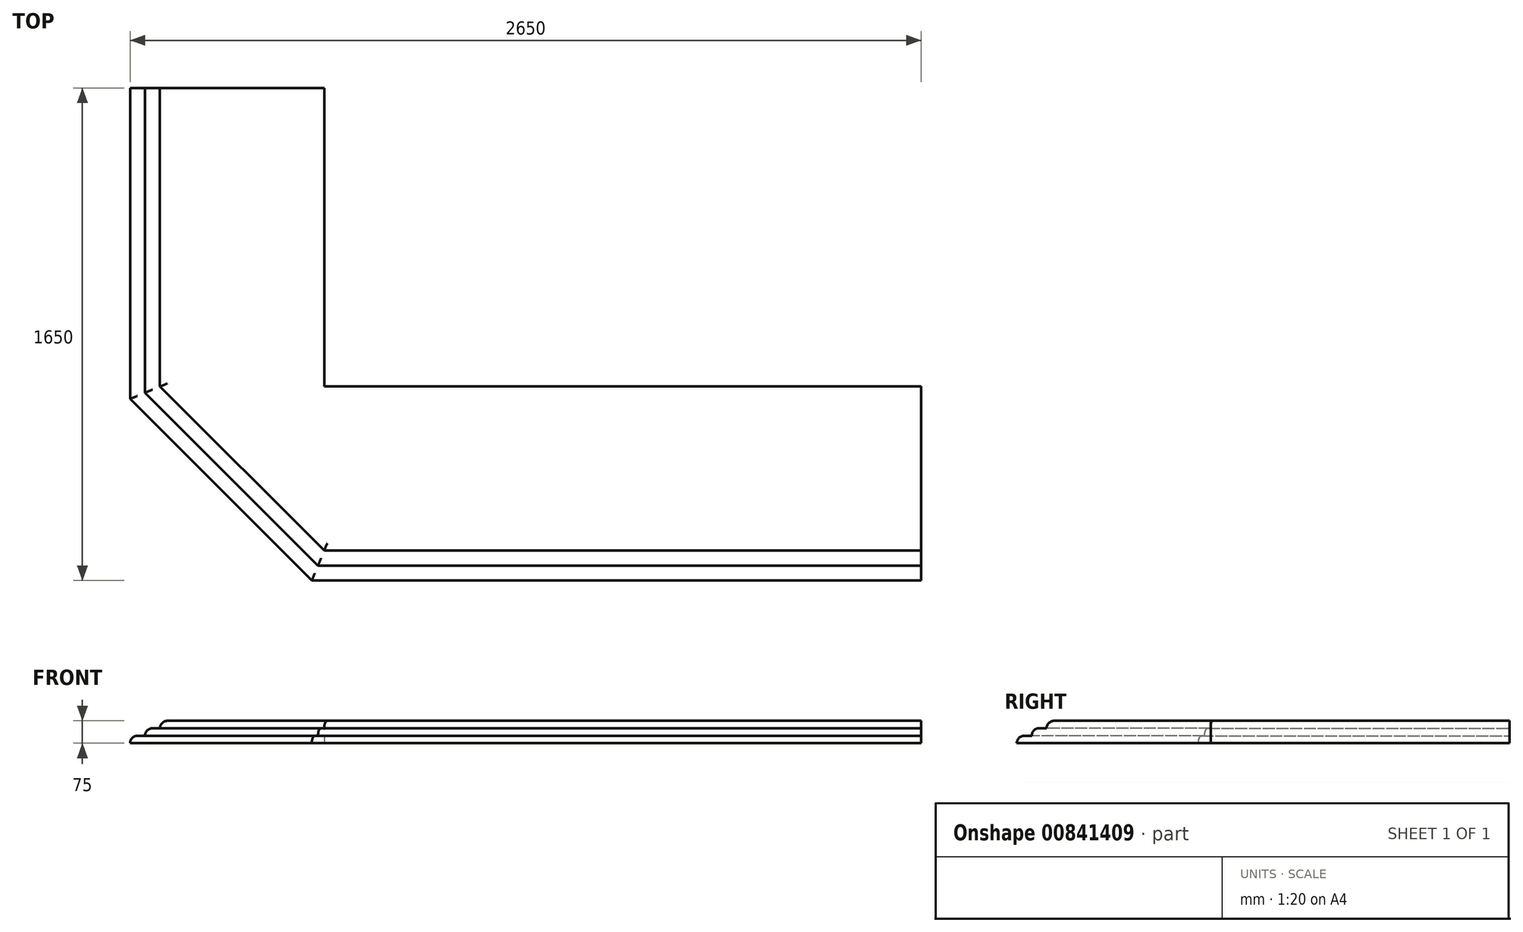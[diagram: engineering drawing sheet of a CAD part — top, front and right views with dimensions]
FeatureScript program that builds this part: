
annotation { "Feature Type Name" : "Feature", "Feature Type Description" : "" }
export const myFeature = defineFeature(function(context is Context, id is Id, definition is map)
    precondition{}
    {
        {
            var Q0;
            Q0=qCreatedBy(makeId("Top.planeOp"),FACE);
            var sketch = newSketch(context, id + "F0", { "sketchPlane" : qUnion([Q0])});
            skLineSegment(sketch, "E0.right", {"start": v(-1000, 500) * mm, "end": v(-1000, -500) * mm});
            skPoint(sketch, "E0.middle", {"position": v(0, 0) * mm});
            skLineSegment(sketch, "E1.bottom", {"start": v(-1000, -1050) * mm, "end": v(1000, -1050) * mm});
            skLineSegment(sketch, "E1.left", {"start": v(-1550, -500) * mm, "end": v(-1550, 500) * mm});
            skLineSegment(sketch, "E2", {"start": v(-1000, 500) * mm, "end": v(-1550, 500) * mm});
            skLineSegment(sketch, "E3", {"start": v(1000, -500) * mm, "end": v(1000, -1050) * mm});
            skLineSegment(sketch, "E4", {"start": v(1000, -500) * mm, "end": v(-1000, -500) * mm});
            skLineSegment(sketch, "E5", {"start": v(-1550, -500) * mm, "end": v(-1000, -1050) * mm});
            skPoint(sketch, "E6.orphan", {"position": v(-1550, 1050) * mm});
            skPoint(sketch, "E1.right.end.orphan", {"position": v(1550, 1050) * mm});
            skPoint(sketch, "E7.orphan", {"position": v(1550, -1050) * mm});
            skPoint(sketch, "E0.left.start.orphan", {"position": v(1000, 500) * mm});
            skPoint(sketch, "E8.orphan", {"position": v(-1550, -1050) * mm});
            skSolve(sketch);
        }
        {
            var Q0;
            Q0 = qSketchRegion(id + "F0", true);
            extrude(context, id + "F1", {"entities" : qUnion([Q0]), "depth" : 25 * mm, "offsetDistance" : 25 * mm});
        }
        {
            var Q0;
            Q0=makeQuery(id+"F1.opExtrude","CAP_FACE",FACE,{"disambiguationData":[OSD([sQuery(id+"F0.wireOp",EDGE,"E0.right"),sQuery(id+"F0.wireOp",EDGE,"E1.bottom"),sQuery(id+"F0.wireOp",EDGE,"E1.left"),sQuery(id+"F0.wireOp",EDGE,"E2"),sQuery(id+"F0.wireOp",EDGE,"E3"),sQuery(id+"F0.wireOp",EDGE,"E4"),sQuery(id+"F0.wireOp",EDGE,"E5")])],"isStart":true});
            var sketch = newSketch(context, id + "F2", { "sketchPlane" : qUnion([Q0])});
            skLineSegment(sketch, "E9.0", {"start": v(-1600, 520.71) * mm, "end": v(-1600, -550) * mm});
            skLineSegment(sketch, "E9.1", {"start": v(-950, -550) * mm, "end": v(-1600, -550) * mm});
            skLineSegment(sketch, "E9.2", {"start": v(-1020.71, 1100) * mm, "end": v(1050, 1100) * mm});
            skLineSegment(sketch, "E9.3", {"start": v(1050, 450) * mm, "end": v(1050, 1100) * mm});
            skLineSegment(sketch, "E9.4", {"start": v(1050, 450) * mm, "end": v(-950, 450) * mm});
            skLineSegment(sketch, "E9.5", {"start": v(-1600, 520.71) * mm, "end": v(-1020.71, 1100) * mm});
            skLineSegment(sketch, "E9.6", {"start": v(-950, -550) * mm, "end": v(-950, 450) * mm});
            skSolve(sketch);
        }
        {
            var Q0;
            Q0 = qSketchRegion(id + "F2", true);
            extrude(context, id + "F3", {"entities" : qUnion([Q0]), "operationType" : NewBodyOperationType.ADD, "depth" : 25 * mm, "offsetDistance" : 25 * mm});
        }
        {
            var Q0;
            Q0=makeQuery(id+"F3.opExtrude","CAP_FACE",FACE,{"disambiguationData":[OSD([sQuery(id+"F2.wireOp",EDGE,"E9.0"),sQuery(id+"F2.wireOp",EDGE,"E9.1"),sQuery(id+"F2.wireOp",EDGE,"E9.2"),sQuery(id+"F2.wireOp",EDGE,"E9.3"),sQuery(id+"F2.wireOp",EDGE,"E9.4"),sQuery(id+"F2.wireOp",EDGE,"E9.5"),sQuery(id+"F2.wireOp",EDGE,"E9.6")])],"isStart":false});
            var sketch = newSketch(context, id + "F4", { "sketchPlane" : qUnion([Q0])});
            skLineSegment(sketch, "E10.0", {"start": v(-1650, 541.42) * mm, "end": v(-1650, -600) * mm});
            skLineSegment(sketch, "E10.1", {"start": v(-900, -600) * mm, "end": v(-1650, -600) * mm});
            skLineSegment(sketch, "E10.2", {"start": v(-1041.42, 1150) * mm, "end": v(1100, 1150) * mm});
            skLineSegment(sketch, "E10.3", {"start": v(1100, 400) * mm, "end": v(1100, 1150) * mm});
            skLineSegment(sketch, "E10.4", {"start": v(1100, 400) * mm, "end": v(-900, 400) * mm});
            skLineSegment(sketch, "E10.5", {"start": v(-1650, 541.42) * mm, "end": v(-1041.42, 1150) * mm});
            skLineSegment(sketch, "E10.6", {"start": v(-900, -600) * mm, "end": v(-900, 400) * mm});
            skSolve(sketch);
        }
        {
            var Q0;
            Q0 = qSketchRegion(id + "F4", true);
            extrude(context, id + "F5", {"entities" : qUnion([Q0]), "operationType" : NewBodyOperationType.ADD, "depth" : 25 * mm, "offsetDistance" : 25 * mm});
        }
        {
            var Q0;
            Q0=makeQuery(id+"F1.opExtrude","CAP_FACE",FACE,{"disambiguationData":[OSD([sQuery(id+"F0.wireOp",EDGE,"E0.right"),sQuery(id+"F0.wireOp",EDGE,"E1.bottom"),sQuery(id+"F0.wireOp",EDGE,"E1.left"),sQuery(id+"F0.wireOp",EDGE,"E2"),sQuery(id+"F0.wireOp",EDGE,"E3"),sQuery(id+"F0.wireOp",EDGE,"E4"),sQuery(id+"F0.wireOp",EDGE,"E5")])],"isStart":false});
            var sketch = newSketch(context, id + "F6", { "sketchPlane" : qUnion([Q0])});
            skLineSegment(sketch, "E11", {"start": v(-1946.23, 500) * mm, "end": v(-1000, 500) * mm});
            skLineSegment(sketch, "E12", {"start": v(-1000, 500) * mm, "end": v(-1000, -500) * mm});
            skLineSegment(sketch, "E13", {"start": v(-1000, -500) * mm, "end": v(1000, -500) * mm});
            skLineSegment(sketch, "E14", {"start": v(1000, -500) * mm, "end": v(1000, -1340.44) * mm});
            skLineSegment(sketch, "E15", {"start": v(1000, -1340.44) * mm, "end": v(1594.24, -1340.44) * mm});
            skLineSegment(sketch, "E16", {"start": v(1594.24, -1340.44) * mm, "end": v(1594.24, 705.58) * mm});
            skLineSegment(sketch, "E17", {"start": v(1594.24, 705.58) * mm, "end": v(-1950.95, 705.58) * mm});
            skLineSegment(sketch, "E18", {"start": v(-1950.95, 705.58) * mm, "end": v(-1946.23, 500) * mm});
            skSolve(sketch);
        }
        {
            var Q0;
            Q0 = qSketchRegion(id + "F6", true);
            extrude(context, id + "F7", {"entities" : qUnion([Q0]), "operationType" : NewBodyOperationType.REMOVE, "oppositeDirection" : true, "depth" : 720 * mm, "offsetDistance" : 25 * mm});
        }
        {
            var Q0;
            Q0=makeQuery(id+"F1.opExtrude","CAP_EDGE",EDGE,{"disambiguationData":[OSD([sQuery(id+"F0.wireOp",EDGE,"E1.left")])],"isStart":false});
            var Q1;
            Q1=makeQuery(id+"F3.opExtrude","CAP_EDGE",EDGE,{"disambiguationData":[OSD([sQuery(id+"F2.wireOp",EDGE,"E9.0")])],"isStart":true});
            var Q2;
            Q2=makeQuery(id+"F5.opExtrude","CAP_EDGE",EDGE,{"disambiguationData":[OSD([sQuery(id+"F4.wireOp",EDGE,"E10.0")])],"isStart":true});
            var Q3;
            Q3=makeQuery(id+"F1.opExtrude","CAP_EDGE",EDGE,{"disambiguationData":[OSD([sQuery(id+"F0.wireOp",EDGE,"E5")])],"isStart":false});
            var Q4;
            Q4=makeQuery(id+"F3.opExtrude","CAP_EDGE",EDGE,{"disambiguationData":[OSD([sQuery(id+"F2.wireOp",EDGE,"E9.5")])],"isStart":true});
            var Q5;
            Q5=makeQuery(id+"F5.opExtrude","CAP_EDGE",EDGE,{"disambiguationData":[OSD([sQuery(id+"F4.wireOp",EDGE,"E10.5")])],"isStart":true});
            var Q6;
            Q6=makeQuery(id+"F1.opExtrude","CAP_EDGE",EDGE,{"disambiguationData":[OSD([sQuery(id+"F0.wireOp",EDGE,"E1.bottom")])],"isStart":false});
            var Q7;
            Q7=makeQuery(id+"F3.opExtrude","CAP_EDGE",EDGE,{"disambiguationData":[OSD([sQuery(id+"F2.wireOp",EDGE,"E9.2")])],"isStart":true});
            var Q8;
            Q8=makeQuery(id+"F5.opExtrude","CAP_EDGE",EDGE,{"disambiguationData":[OSD([sQuery(id+"F4.wireOp",EDGE,"E10.2")])],"isStart":true});
            fillet(context, id + "F8", {"entities" : qUnion([Q0, Q1, Q2, Q3, Q4, Q5, Q6, Q7, Q8]), "radius" : 25 * mm, "tangentPropagation" : true, "allowEdgeOverflow" : false});
        }
    });
